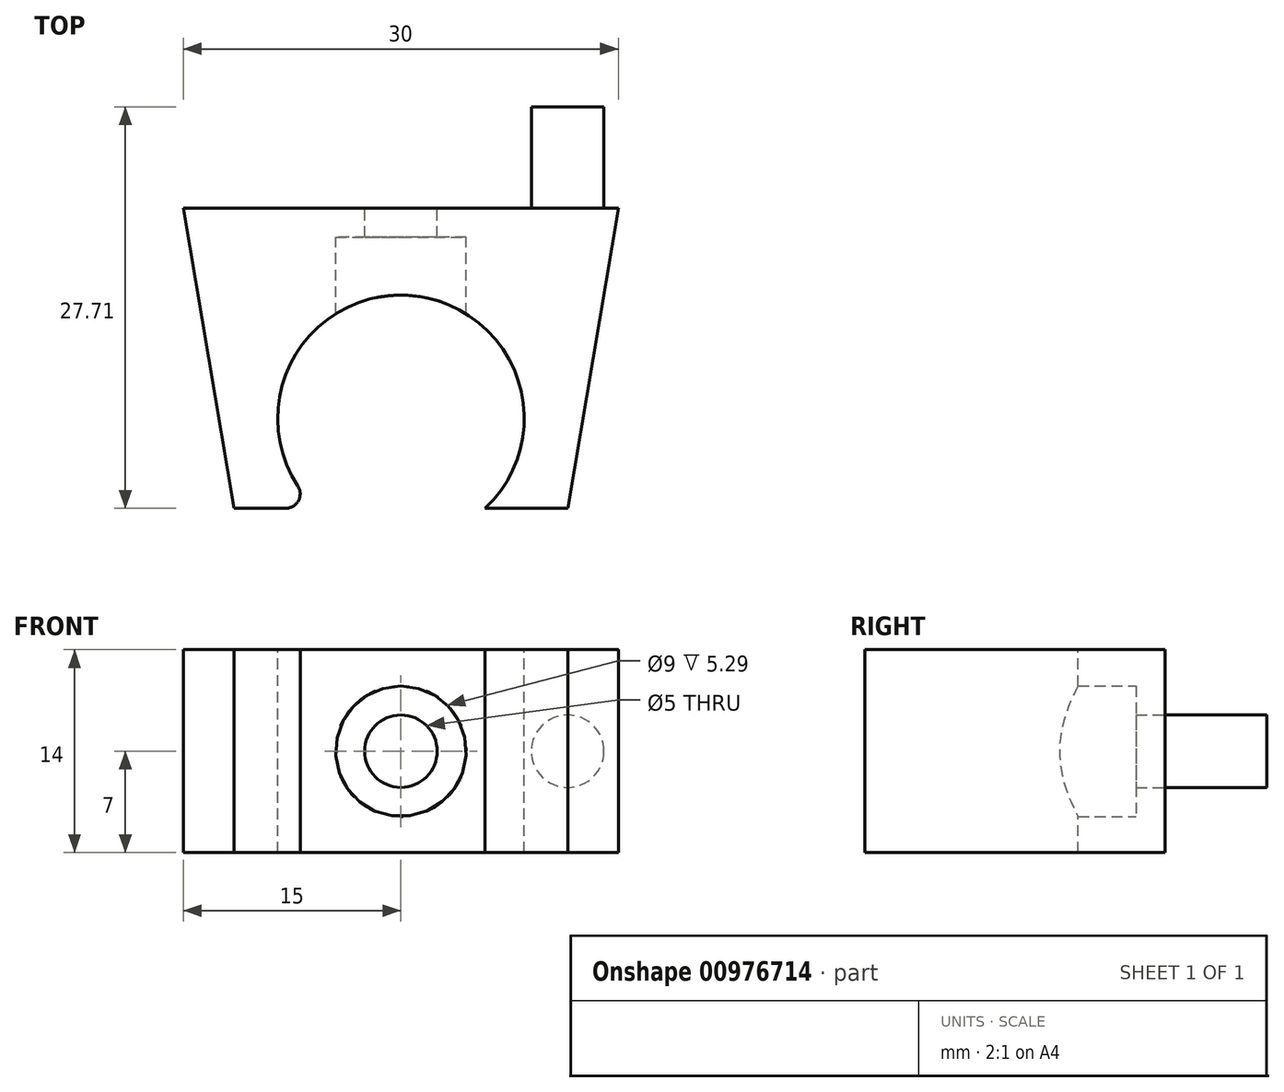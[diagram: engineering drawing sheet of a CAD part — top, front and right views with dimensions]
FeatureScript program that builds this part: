
annotation { "Feature Type Name" : "Feature", "Feature Type Description" : "" }
export const myFeature = defineFeature(function(context is Context, id is Id, definition is map)
    precondition{}
    {
        {
            var Q0;
            Q0=qCreatedBy(makeId("Top.planeOp"),FACE);
            var sketch = newSketch(context, id + "F0", { "sketchPlane" : qUnion([Q0])});
            skLineSegment(sketch, "E0", {"start": v(-15, 0) * mm, "end": v(-11.5, -20.7) * mm});
            skLineSegment(sketch, "E1", {"start": v(-11.5, -20.7) * mm, "end": v(11.5, -20.7) * mm});
            skLineSegment(sketch, "E2", {"start": v(11.5, -20.7) * mm, "end": v(15, 0) * mm});
            skLineSegment(sketch, "E3", {"start": v(15, 0) * mm, "end": v(-15, 0) * mm});
            skSolve(sketch);
        }
        {
            var Q0;
            Q0 = qSketchRegion(id + "F0", true);
            extrude(context, id + "F1", {"entities" : qUnion([Q0]), "depth" : 14 * mm, "offsetDistance" : 25 * mm});
        }
        {
            var Q0;
            Q0=makeQuery(id+"F1.opExtrude","SWEPT_FACE",FACE,{"disambiguationData":[OSD([sQuery(id+"F0.wireOp",EDGE,"E3")])]});
            var sketch = newSketch(context, id + "F2", { "sketchPlane" : qUnion([Q0])});
            skLineSegment(sketch, "E4", {"start": v(15, 14) * mm, "end": v(-15, 0) * mm, "construction": true});
            skLineSegment(sketch, "E5", {"start": v(-15, 0) * mm, "end": v(-15, 14) * mm});
            skLineSegment(sketch, "E6", {"start": v(-15, 14) * mm, "end": v(15, 0) * mm, "construction": true});
            skPoint(sketch, "E7", {"position": v(0, 7) * mm});
            skSolve(sketch);
        }
        {
            var Q0;
            Q0=sQuery(id+"F2.wireOp",VERTEX,"E7");
            var Q1;
            Q1=makeQuery(id+"F1.opExtrude","SWEPT_BODY",BODY,{"disambiguationData":[OSD([sQuery(id+"F0.wireOp",EDGE,"E0"),sQuery(id+"F0.wireOp",EDGE,"E1"),sQuery(id+"F0.wireOp",EDGE,"E2"),sQuery(id+"F0.wireOp",EDGE,"E3")])]});
            hole(context, id + "F3", {"style" : HoleStyle.SIMPLE, "endStyle" : HoleEndStyle.THROUGH, "holeDiameter" : 9 * mm, "majorDiameter" : 5 * mm, "isTappedThrough" : true, "tappedDepth" : 4 * mm, "tapClearance" : 3, "locations" : qUnion([Q0]), "scope" : qUnion([Q1])});
        }
        {
            var Q0;
            Q0=makeQuery(id+"F1.opExtrude","CAP_FACE",FACE,{"disambiguationData":[OSD([sQuery(id+"F0.wireOp",EDGE,"E0"),sQuery(id+"F0.wireOp",EDGE,"E1"),sQuery(id+"F0.wireOp",EDGE,"E2"),sQuery(id+"F0.wireOp",EDGE,"E3")])],"isStart":false});
            var sketch = newSketch(context, id + "F4", { "sketchPlane" : qUnion([Q0])});
            skCircle(sketch, "E8", {"center": v(0, -14.5) * mm, "radius": 8.5 * mm});
            skSolve(sketch);
        }
        {
            var Q0;
            {var subQ0=sQuery(id+"F4.wireOp",EDGE,"E8");var subQ1=makeQuery(id+"F1.opExtrude","CAP_EDGE",EDGE,{"disambiguationData":[OSD([sQuery(id+"F0.wireOp",EDGE,"E1")])],"isStart":false});var subQ2=makeQuery(id+"F4.imprint","INTERSECT",VERTEX,{"disambiguationData":[OD(0.0)],"derivedFrom":[subQ1,subQ0]});Q0=makeQuery(id+"F4.imprint","IMPRINT",FACE,{"disambiguationData":[TD([[makeQuery(id+"F4.imprint","IMPRINT",EDGE,{"disambiguationData":[TD([[subQ2,1.0]])],"derivedFrom":subQ0}),1.0]])]});}
            extrude(context, id + "F5", {"entities" : qUnion([Q0]), "operationType" : NewBodyOperationType.REMOVE, "oppositeDirection" : true, "depth" : 25 * mm, "offsetDistance" : 25 * mm});
        }
        {
            var Q0;
            Q0=makeQuery(id+"F1.opExtrude","SWEPT_FACE",FACE,{"disambiguationData":[OSD([sQuery(id+"F0.wireOp",EDGE,"E3")])]});
            var sketch = newSketch(context, id + "F6", { "sketchPlane" : qUnion([Q0])});
            skCircle(sketch, "E9", {"center": v(0, 7) * mm, "radius": 5.1 * mm});
            skSolve(sketch);
        }
        {
            var Q0;
            Q0 = qSketchRegion(id + "F6", true);
            extrude(context, id + "F7", {"entities" : qUnion([Q0]), "operationType" : NewBodyOperationType.ADD, "oppositeDirection" : true, "depth" : 2 * mm, "offsetDistance" : 25 * mm});
        }
        {
            var Q0;
            Q0=makeQuery(id+"F7.boolean.opBoolean","MERGE",FACE,{"derivedFrom":[makeQuery(id+"F1.opExtrude","SWEPT_FACE",FACE,{"disambiguationData":[OSD([sQuery(id+"F0.wireOp",EDGE,"E3")])]}),makeQuery(id+"F7.opExtrude","CAP_FACE",FACE,{"disambiguationData":[OSD([sQuery(id+"F6.wireOp",EDGE,"E9")])],"isStart":true})]});
            var sketch = newSketch(context, id + "F8", { "sketchPlane" : qUnion([Q0])});
            skLineSegment(sketch, "E10", {"start": v(-15, 0) * mm, "end": v(15, 14) * mm, "construction": true});
            skLineSegment(sketch, "E11", {"start": v(15, 0) * mm, "end": v(-15, 14) * mm, "construction": true});
            skPoint(sketch, "E12", {"position": v(0, 7) * mm});
            skPoint(sketch, "E13", {"position": v(-11.5, 7) * mm});
            skCircle(sketch, "E14", {"center": v(-11.5, 7) * mm, "radius": 2.5 * mm});
            skSolve(sketch);
        }
        {
            var Q0;
            Q0=sQuery(id+"F8.wireOp",VERTEX,"E12");
            var Q1;
            Q1=makeQuery(id+"F1.opExtrude","SWEPT_BODY",BODY,{"disambiguationData":[OSD([sQuery(id+"F0.wireOp",EDGE,"E0"),sQuery(id+"F0.wireOp",EDGE,"E1"),sQuery(id+"F0.wireOp",EDGE,"E2"),sQuery(id+"F0.wireOp",EDGE,"E3")])]});
            hole(context, id + "F9", {"style" : HoleStyle.SIMPLE, "endStyle" : HoleEndStyle.THROUGH, "holeDiameter" : 5 * mm, "majorDiameter" : 5 * mm, "isTappedThrough" : true, "tappedDepth" : 4 * mm, "tapClearance" : 3, "locations" : qUnion([Q0]), "scope" : qUnion([Q1])});
        }
        {
            var Q0;
            {var subQ0=sQuery(id+"F4.wireOp",EDGE,"E8");var subQ1=sQuery(id+"F0.wireOp",EDGE,"E1");Q0=makeQuery(id+"F5.boolean.opBoolean","COPY",EDGE,{"derivedFrom":makeQuery(id+"F5.opExtrude","SWEPT_EDGE",EDGE,{"disambiguationData":[OSD([subQ1,subQ0]),TDD([makeQuery(id+"F4.imprint","INTERSECT",VERTEX,{"disambiguationData":[OD(0.0)],"derivedFrom":[makeQuery(id+"F1.opExtrude","CAP_EDGE",EDGE,{"disambiguationData":[OSD([subQ1])],"isStart":false}),subQ0]})])]})});}
            var Q1;
            {var subQ0=sQuery(id+"F4.wireOp",EDGE,"E8");var subQ1=sQuery(id+"F0.wireOp",EDGE,"E1");Q1=makeQuery(id+"F5.boolean.opBoolean","COPY",EDGE,{"derivedFrom":makeQuery(id+"F5.opExtrude","SWEPT_EDGE",EDGE,{"disambiguationData":[OSD([subQ1,subQ0]),TDD([makeQuery(id+"F4.imprint","INTERSECT",VERTEX,{"disambiguationData":[OD(1.0)],"derivedFrom":[makeQuery(id+"F1.opExtrude","CAP_EDGE",EDGE,{"disambiguationData":[OSD([subQ1])],"isStart":false}),subQ0]})])]})});}
            fillet(context, id + "F10", {"entities" : qUnion([Q0, Q1]), "radius" : 1 * mm, "tangentPropagation" : true, "allowEdgeOverflow" : false});
        }
        {
            var Q0;
            Q0=makeQuery(id+"F8.imprint","IMPRINT",FACE,{"disambiguationData":[TD([[makeQuery(id+"F8.imprint","IMPRINT",EDGE,{"derivedFrom":sQuery(id+"F8.wireOp",EDGE,"E14")}),1.0]])]});
            extrude(context, id + "F11", {"entities" : qUnion([Q0]), "operationType" : NewBodyOperationType.ADD, "depth" : 7 * mm, "offsetDistance" : 25 * mm});
        }
    });
